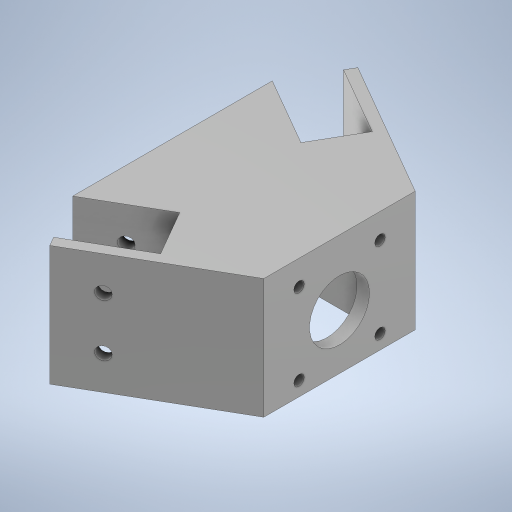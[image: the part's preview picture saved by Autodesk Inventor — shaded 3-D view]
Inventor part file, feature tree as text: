
AUTODESK INVENTOR PART (.ipt)
format: ipt  version: 2024.2 (Build 282272000, 272)  size: 336,384 bytes
history: native  units: mm
features: extrude x8, sketch x8
ambient origin geometry x8: Origin, YZ Plane, XZ Plane, XY Plane, X Axis, Y Axis, Z Axis, Center Point
bodies: Solid1 (feature_tree)
feature tree (16):
  extrude  "Extrusion1"  TaperAngle=150.0deg  [1 undecoded]
  extrude  "Extrusion2"  Depth=43.0mm
  extrude  "Extrusion3"  Depth=20.0mm
  extrude  "Extrusion4"  Depth=4.0mm
  extrude  "Extrusion5"  Depth=4.0mm TaperAngle=0.0deg
  extrude  "Extrusion6"  Depth=23.0mm
  sketch  "Sketch7"  dims[d20=31.0mm d21=31.0mm]
  extrude  "Extrusion7"  Depth=31.0mm
  extrude  "Extrusion8"  Depth=4.0mm
  sketch  "Sketch1"  dims[d1=60.0deg d3=150.0deg]
  sketch  "Sketch2"  dims[d4=43.0mm d6=55.0mm]
  sketch  "Sketch3"  dims[d8=20.0mm d9=20.0mm]
  sketch  "Sketch4"  dims[d10=4.0mm d11=4.0mm]
  sketch  "Sketch5"  dims[d14=46.0mm d15=0.0mm d16=4.0mm d17=0.0mm]
  sketch  "Sketch6"  dims[d18=21.0mm d19=23.0mm]
  sketch  "Sketch8"  dims[d22=4.0mm d23=4.0mm d24=4.0mm d25=4.0mm d29=46.0mm d30=0.0mm d32=0.0mm d33=0.0mm d34=20.0mm d35=15.0mm d36=13.0mm d37=5.0mm d38=5.0mm d39=10.0mm d40=0.0mm d41=20.0mm d42=10.0mm d43=15.0mm d44=5.0mm d45=5.0mm d46=0.0mm d47=0.0mm d48=5.0mm d49=5.0mm d50=10.0mm d51=0.0mm d52=10.0mm d53=0.0mm d54=58.0mm d55=60.0mm d56=30.0mm d57=30.0mm]
note: 1 required parameter value undecoded (feature->parameter linkage not recoverable at this tier; creation-order binding heuristic only, values carry confidence <= 0.55)
